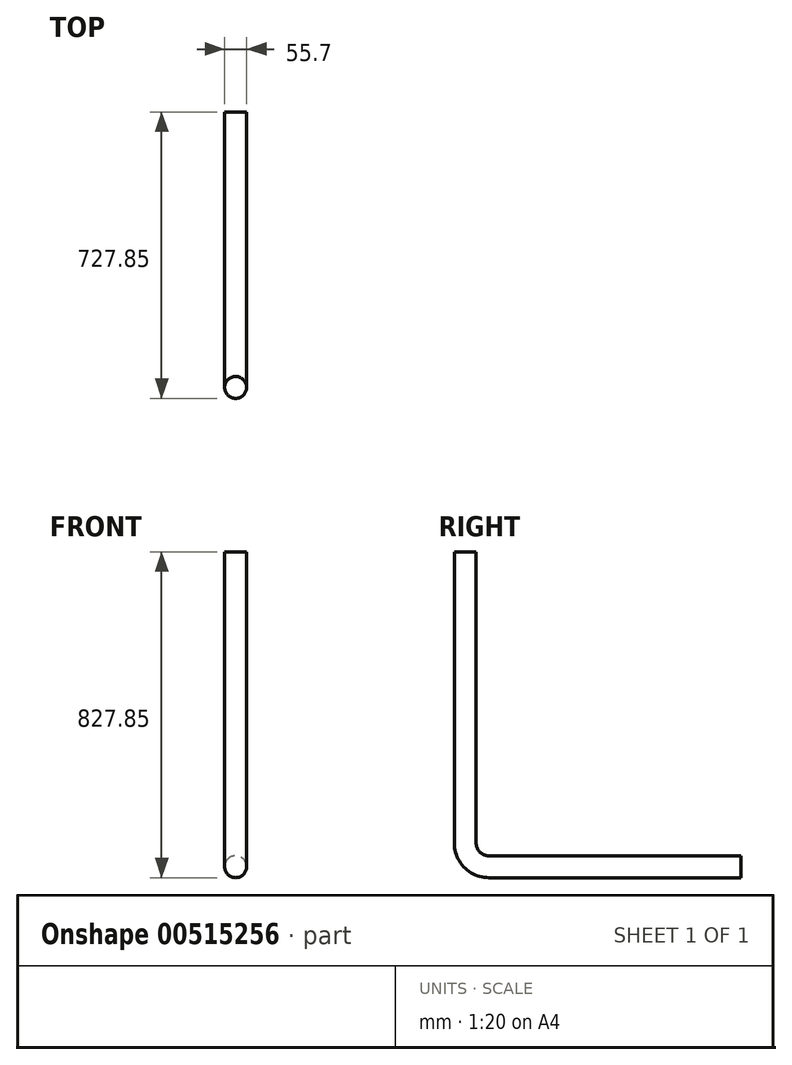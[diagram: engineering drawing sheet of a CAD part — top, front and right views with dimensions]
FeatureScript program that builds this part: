
annotation { "Feature Type Name" : "Feature", "Feature Type Description" : "" }
export const myFeature = defineFeature(function(context is Context, id is Id, definition is map)
    precondition{}
    {
        {
            var Q0;
            Q0=qCreatedBy(makeId("Right.planeOp"),FACE);
            var sketch = newSketch(context, id + "F0", { "sketchPlane" : qUnion([Q0])});
            skLineSegment(sketch, "E0", {"start": v(0, 800) * mm, "end": v(0, 60) * mm});
            skLineSegment(sketch, "E1", {"start": v(60, 0) * mm, "end": v(700, 0) * mm});
            skPoint(sketch, "E2.visualSharp", {"position": v(0, 0) * mm});
            skArc(sketch, "E2.filletArc", {"start": v(0, 60) * mm, "mid": v(17.57, 17.57) * mm, "end": v(60, 0) * mm});
            skSolve(sketch);
        }
        {
            var Q0;
            Q0=sQuery(id+"F0.wireOp",VERTEX,"E0.start");
            var Q1;
            Q1=qCreatedBy(makeId("Top.planeOp"),FACE);
            cPlane(context, id + "F1", {"entities" : qUnion([Q0, Q1]), "cplaneType" : CPlaneType.PLANE_POINT, "offset" : 25 * mm, "width" : 150 * mm, "height" : 150 * mm});
        }
        {
            var Q0;
            Q0=qCreatedBy(id+"F1.planeOp",FACE);
            var sketch = newSketch(context, id + "F2", { "sketchPlane" : qUnion([Q0])});
            skCircle(sketch, "E3", {"center": v(0, 0) * mm, "radius": 27.85 * mm});
            skSolve(sketch);
        }
        {
            var Q0;
            Q0=makeQuery(id+"F2.imprint","IMPRINT",FACE,{"disambiguationData":[TD([[makeQuery(id+"F2.imprint","IMPRINT",EDGE,{"derivedFrom":sQuery(id+"F2.wireOp",EDGE,"E3")}),1.0]])]});
            var Q1;
            Q1=sQuery(id+"F0.wireOp",EDGE,"E0");
            var Q2;
            Q2=sQuery(id+"F0.wireOp",EDGE,"E2.filletArc");
            var Q3;
            Q3=sQuery(id+"F0.wireOp",EDGE,"E1");
            sweep(context, id + "F3", {"profiles" : qUnion([Q0]), "path" : qUnion([Q1, Q2, Q3])});
        }
    });
